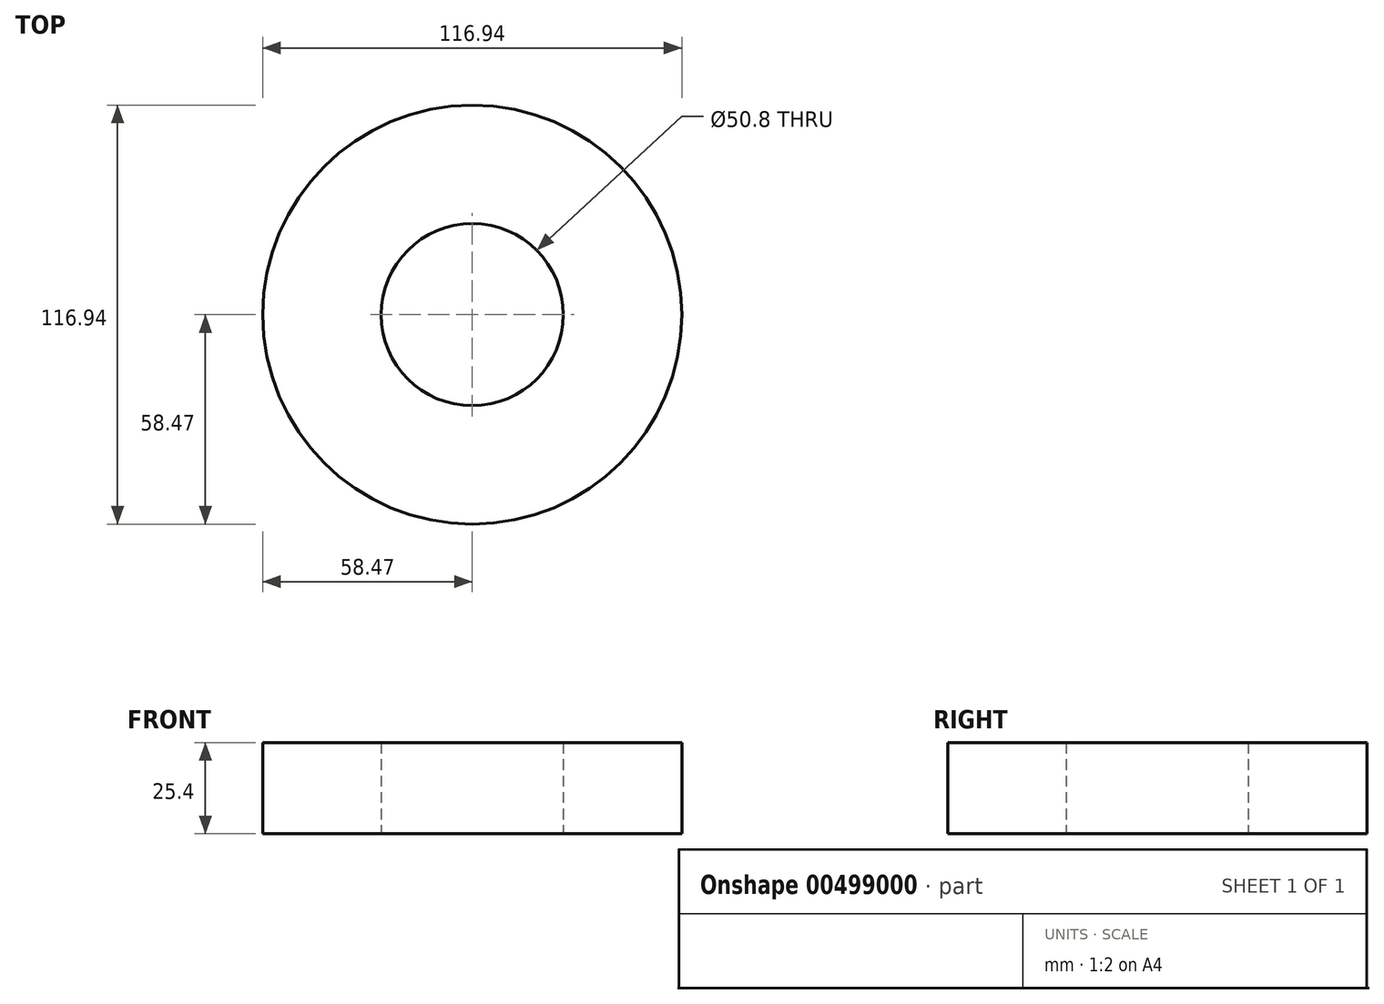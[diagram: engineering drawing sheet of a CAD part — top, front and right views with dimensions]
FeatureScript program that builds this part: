
annotation { "Feature Type Name" : "Feature", "Feature Type Description" : "" }
export const myFeature = defineFeature(function(context is Context, id is Id, definition is map)
    precondition{}
    {
        {
            var Q0;
            Q0=qCreatedBy(makeId("Top.planeOp"),FACE);
            var sketch = newSketch(context, id + "F0", { "sketchPlane" : qUnion([Q0])});
            skCircle(sketch, "E0", {"center": v(0, 0) * mm, "radius": 25.4 * mm});
            skCircle(sketch, "E1", {"center": v(0, 0) * mm, "radius": 58.47 * mm});
            skCircle(sketch, "E2", {"center": v(0, 0) * mm, "radius": 10 * mm});
            skSolve(sketch);
        }
        {
            var Q0;
            Q0=makeQuery(id+"F0.imprint","IMPRINT",FACE,{"disambiguationData":[TD([[makeQuery(id+"F0.imprint","IMPRINT",EDGE,{"derivedFrom":sQuery(id+"F0.wireOp",EDGE,"E0")}),-1.0]])]});
            extrude(context, id + "F1", {"entities" : qUnion([Q0]), "depth" : 25.4 * mm});
        }
    });
